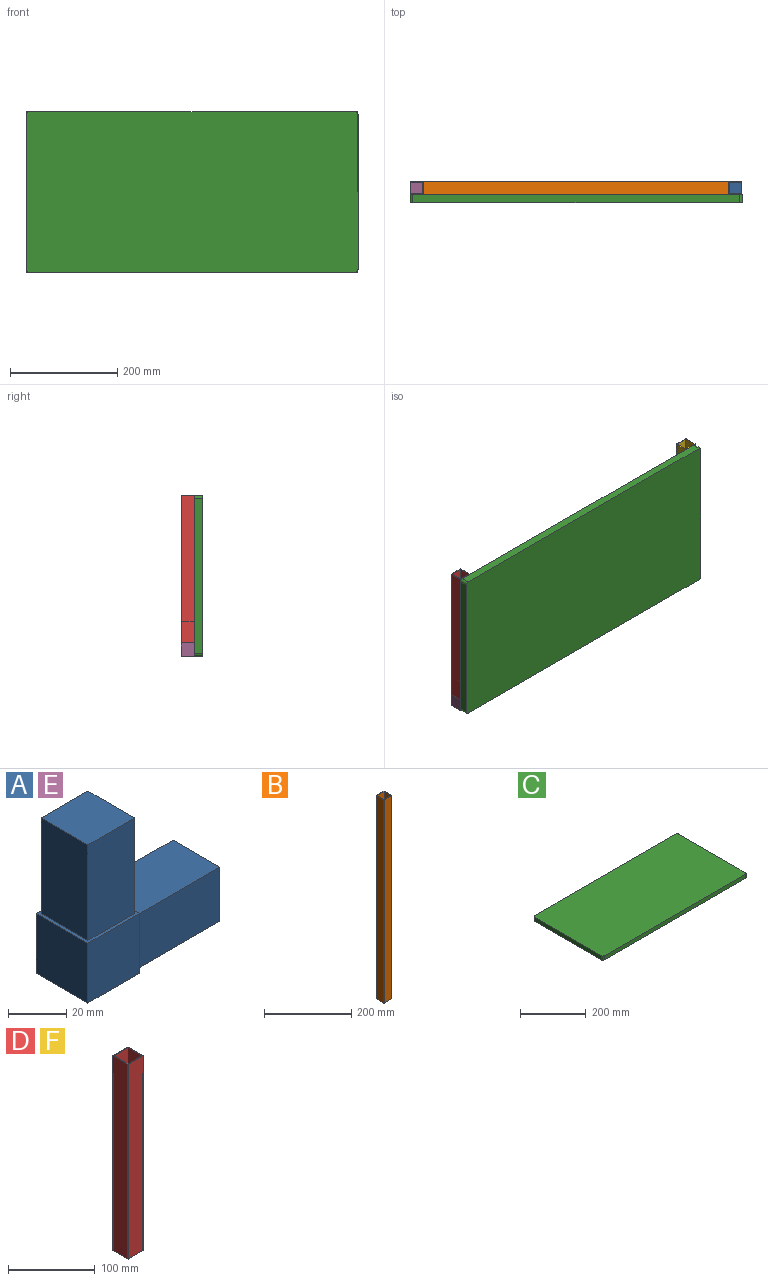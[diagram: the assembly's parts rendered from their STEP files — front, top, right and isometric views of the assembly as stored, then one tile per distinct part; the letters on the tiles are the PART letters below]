
ASSEMBLY  parts=6 mates=16
PART A: 16 faces, bbox 65x25x65 mm
  f0: plane 25x25mm, normal (0,0,1), area 114.2mm2, adj f1,f2,f3,f4,f11,f12,f13,f14
  f1: plane 25x25mm, normal (1,0,0), area 114.2mm2, adj f0,f2,f4,f5,f6,f7,f8,f9
  f2: plane 25x25mm, normal (0,1,0), area 625mm2, adj f0,f1,f3,f5
  f3: plane 25x25mm, normal (-1,0,0), area 625mm2, adj f0,f2,f4,f5
  f4: plane 25x25mm, normal (0,-1,0), area 625mm2, adj f0,f1,f3,f5
  f5: plane 25x25mm, normal (0,0,-1), area 625mm2, adj f1,f2,f3,f4
  f6: plane 40x22.6mm, normal (0,0,1), area 904mm2, adj f1,f7,f9,f10
  f7: plane 40x22.6mm, normal (0,-1,0), area 904mm2, adj f1,f6,f8,f10
  f8: plane 40x22.6mm, normal (0,0,-1), area 904mm2, adj f1,f7,f9,f10
  f9: plane 40x22.6mm, normal (0,1,0), area 904mm2, adj f1,f6,f8,f10
  f10: plane 22.6x22.6mm, normal (1,0,0), area 510.8mm2, adj f6,f7,f8,f9
  f11: plane 40x22.6mm, normal (-1,0,0), area 904mm2, adj f0,f12,f14,f15
  f12: plane 40x22.6mm, normal (0,-1,0), area 904mm2, adj f0,f11,f13,f15
  f13: plane 40x22.6mm, normal (1,0,0), area 904mm2, adj f0,f12,f14,f15
  f14: plane 40x22.6mm, normal (0,1,0), area 904mm2, adj f0,f11,f13,f15
  f15: plane 22.6x22.6mm, normal (0,0,1), area 510.8mm2, adj f11,f12,f13,f14
PART B: 14 faces, bbox 25x25x570 mm
  f0: plane 570x23.6mm, normal (0,1,0), area 13452mm2, adj f8,f9,f10,f13
  f1: plane 570x23.6mm, normal (-1,0,0), area 13452mm2, adj f8,f9,f10,f11
  f2: plane 570x23.6mm, normal (0,-1,0), area 13452mm2, adj f8,f9,f11,f12
  f3: plane 570x22.6mm, normal (1,0,0), area 12882mm2, adj f4,f6,f8,f9
  f4: plane 570x22.6mm, normal (0,-1,0), area 12882mm2, adj f3,f5,f8,f9
  f5: plane 570x22.6mm, normal (-1,0,0), area 12882mm2, adj f4,f6,f8,f9
  f6: plane 570x22.6mm, normal (0,1,0), area 12882mm2, adj f3,f5,f8,f9
  f7: plane 570x23.6mm, normal (1,0,0), area 13452mm2, adj f8,f9,f12,f13
  f8: plane 25x25mm, normal (0,0,1), area 113.8mm2, adj f0,f1,f2,f3,f4,f5,f6,f7
  f9: plane 25x25mm, normal (0,0,-1), area 113.8mm2, adj f0,f1,f2,f3,f4,f5,f6,f7
  f10: cylinder r=0.7mm len=570mm, axis (0,0,1), area 626.7mm2, adj f0,f1,f8,f9
  f11: cylinder r=0.7mm len=570mm, axis (0,0,-1), area 626.7mm2, adj f1,f2,f8,f9
  f12: cylinder r=0.7mm len=570mm, axis (0,0,1), area 626.7mm2, adj f2,f7,f8,f9
  f13: cylinder r=0.7mm len=570mm, axis (0,0,-1), area 626.7mm2, adj f0,f7,f8,f9
PART C: 10 faces, bbox 620x300x15 mm
  f0: plane 610x15mm, normal (0,1,0), area 9150mm2, adj f4,f5,f6,f9
  f1: plane 290x15mm, normal (-1,0,0), area 4350mm2, adj f4,f5,f6,f7
  f2: plane 610x15mm, normal (0,-1,0), area 9150mm2, adj f4,f5,f7,f8
  f3: plane 290x15mm, normal (1,0,0), area 4350mm2, adj f4,f5,f8,f9
  f4: plane 620x300mm, normal (0,0,1), area 185978.5mm2, adj f0,f1,f2,f3,f6,f7,f8,f9
  f5: plane 620x300mm, normal (0,0,-1), area 185978.5mm2, adj f0,f1,f2,f3,f6,f7,f8,f9
  f6: cylinder r=5mm len=15mm, axis (0,0,1), area 117.8mm2, adj f0,f1,f4,f5
  f7: cylinder r=5mm len=15mm, axis (0,0,-1), area 117.8mm2, adj f1,f2,f4,f5
  f8: cylinder r=5mm len=15mm, axis (0,0,1), area 117.8mm2, adj f2,f3,f4,f5
  f9: cylinder r=5mm len=15mm, axis (0,0,-1), area 117.8mm2, adj f0,f3,f4,f5
PART D: 14 faces, bbox 25x25x275 mm
  f0: plane 275x23.6mm, normal (0,1,0), area 6490mm2, adj f8,f9,f10,f13
  f1: plane 275x23.6mm, normal (-1,0,0), area 6490mm2, adj f8,f9,f10,f11
  f2: plane 275x23.6mm, normal (0,-1,0), area 6490mm2, adj f8,f9,f11,f12
  f3: plane 275x22.6mm, normal (1,0,0), area 6215mm2, adj f4,f6,f8,f9
  f4: plane 275x22.6mm, normal (0,-1,0), area 6215mm2, adj f3,f5,f8,f9
  f5: plane 275x22.6mm, normal (-1,0,0), area 6215mm2, adj f4,f6,f8,f9
  f6: plane 275x22.6mm, normal (0,1,0), area 6215mm2, adj f3,f5,f8,f9
  f7: plane 275x23.6mm, normal (1,0,0), area 6490mm2, adj f8,f9,f12,f13
  f8: plane 25x25mm, normal (0,0,1), area 113.8mm2, adj f0,f1,f2,f3,f4,f5,f6,f7
  f9: plane 25x25mm, normal (0,0,-1), area 113.8mm2, adj f0,f1,f2,f3,f4,f5,f6,f7
  f10: cylinder r=0.7mm len=275mm, axis (0,0,1), area 302.4mm2, adj f0,f1,f8,f9
  f11: cylinder r=0.7mm len=275mm, axis (0,0,-1), area 302.4mm2, adj f1,f2,f8,f9
  f12: cylinder r=0.7mm len=275mm, axis (0,0,1), area 302.4mm2, adj f2,f7,f8,f9
  f13: cylinder r=0.7mm len=275mm, axis (0,0,-1), area 302.4mm2, adj f0,f7,f8,f9
PART E: same geometry as A
PART F: same geometry as D
PLACE A rot(axis=(0,0,1),180deg) t=(-411.62,-212.06,-533.62)mm
PLACE B rot(axis=(-0.58,0.58,-0.58),120deg) t=(-1006.62,-187.06,-533.62)mm
PLACE C rot(axis=(0,0.71,-0.71),180deg) t=(-411.62,-212.06,-533.62)mm
PLACE D t=(-1031.62,-187.06,-508.62)mm
PLACE E t=(-1031.62,-187.06,-533.62)mm
PLACE F t=(-436.62,-187.06,-508.62)mm
MATE planar F.f2 <-> D.f2  axis (0,-1,0) through (-424.12,-212.06,-371.12)mm
MATE planar C.f5 <-> B.f7  axis (0,1,0) through (-721.62,-212.06,-383.62)mm
MATE planar E.f4 <-> D.f2  axis (0,-1,0) through (-1019.12,-212.06,-521.12)mm
MATE planar F.f7 <-> A.f3  axis (1,0,0) through (-411.62,-199.56,-371.12)mm
MATE planar E.f3 <-> D.f1  axis (-1,0,0) through (-1031.62,-187.06,-521.12)mm
MATE planar F.f9 <-> A.f0  axis (0,0,-1) through (-424.12,-199.56,-508.62)mm
MATE planar B.f0 <-> E.f5  axis (0,0,-1) through (-721.62,-199.56,-533.62)mm
MATE planar A.f2 <-> B.f7  axis (0,-1,0) through (-424.12,-212.06,-521.12)mm
MATE planar E.f1 <-> B.f9  axis (1,0,0) through (-1006.62,-199.56,-521.12)mm
MATE planar B.f7 <-> E.f4  axis (0,-1,0) through (-721.62,-212.06,-521.12)mm
MATE planar C.f0 <-> B.f0  axis (0,0,-1) through (-721.62,-219.56,-533.62)mm
MATE planar F.f7 <-> C.f1  axis (1,0,0) through (-411.62,-199.56,-371.12)mm
MATE planar B.f0 <-> A.f5  axis (0,0,-1) through (-721.62,-199.56,-533.62)mm
MATE planar E.f0 <-> D.f9  axis (0,0,1) through (-1019.12,-199.56,-508.62)mm
MATE planar A.f1 <-> B.f8  axis (-1,0,0) through (-436.62,-199.56,-521.12)mm
MATE planar D.f8 <-> F.f8  axis (0,0,1) through (-1019.12,-199.56,-233.62)mm
